# Revit family: DBLTD_TheSenatorGroup_OffcChrs_Plum_US
name_source: partatom
category: Furniture
units: mm (PartAtom-declared; Revit-internal decimal feet)

## family parameters
Always vertical = Yes
Cut with Voids When Loaded = No
Room Calculation Point = No
Shared = Yes
Work Plane-Based = No

## types (2) — shared parameters
Assembly Code = E2020200
AssetType = Movable
BIMObjectName = DBLTD_TheSenatorGroup_OfficeChairs_Plum
Category = Pr_40_50_12_57:Office chairs
Color = Defined by Material Specified
Constituents = Plastic glides with felt
DurationUnit = year
ExpectedLife = 5
Features = Soft Seating
Finish = Seat, Back and Arms Upholstered. Frame Black powder coat
FrameFinish = Black powder coat
IfcExportAs = IfcFurnitureType
IfcExportType = CHAIR
IsBuiltIn = No
Keynote = Pr_40_50_12_57
Manufacturer = The Senator Group
ManufacturerName = The Senator Group
ManufacturerURL = https://www.thesenatorgroup.com
Material = Moulded foam construction. Tubular Steel frame.
NBSDescription = Office chairs
NBSReference = 45-35-20/330
Name = OfficeChairs_Plum_TheSenatorGroup
NominalDepth = 26 "
NominalHeight = 30.5 "
PlasticAndMetalFinish = Black powder coat
ProductInformation = https://www.thesenatorgroup.com
SeatDepth = 19.25"
SeatFrameMaterial = TheSenatorGroup_Metal_Black
SeatingHeight = 17.5 "
Status = UNSET
Style = Chair
URL = https://www.thesenatorgroup.com
Uniclass2015Code = Pr_40_50_12_57
Uniclass2015Title = Office chairs
Uniclass2015Version = Products v1.15
Version = 1
WarrantyDescription = Allermuir warrants that its manufactured products are free from manufacturing defects - in materials or workmanship - for a period of five (5) years.
Allermuir will repair, or replace (at Allermuir’s sole discretion) with comparable free of charge materials/ components, any product/ component which fails under normal use in a single shift environment, as a result of a defect in the materials and/or workmanship.

Exceptions -
Non-standard product - 2 years
Screen-mounted Accessories/ Dry-wipe Boards - 2 years
Electrical and/or electronic componentry - 2 years

Exclusions - Allermuir does not warrant:
Failure due to normal “Wear and Tear”.
Natural variations in appearance of wood - its grain, figure and colour.
Changes in surface appearance resulting from exposure to light, and the natural ageing process of wood.
Changes in surface appearance resulting from the misuse of cleaning materials and methods/ damage form sharp objects/ imprinting from writing implements.
Natural variations in Leather - its marks, scars and wrinkles.
Product stored/ exposed to extreme operational conditions.
Consumable components such as Fuses/ Lights/ lamps/ transformers/etc.
Other Manufacturer’s product supplied by Allermuir (their own warranty shall apply where possible).
Non-standard fabrics/ finishes or veneers used. Allermuir only checks the manufacturing quality of Customer’s
Own Material (COM) and provides no warranty for the finish/ fabric itself.
Product which has not been installed/ moved/ reconfigured by Allermuir approved personnel.
Allermuir shall be under no liability whatsoever for any consequential damage, loss or other expenses whether arising out of contract, negligence or otherwise.
WarrantyDurationLabor = 5
WarrantyDurationParts = 5
WarrantyDurationUnit = year
zero-valued in all types: Cost, HighestSeatingHeight, LowestSeatingHeight

## per-type parameters (varying)
| type | HasArms | Model | ModelNumber | NominalLength | NominalWidth | SeatWidth | Size |
| Easy Chair without Arms | No | PLM01 | PLM01 | 23.5 " | 23.5 " | 20.75" | 30.5" (h) x 23.5" (w) x 26" (d) |
| Easy Chair with Arms | Yes | PLM02 | PLM02 | 28.25 " | 28.25 " | 19.25" | 30.5" (h) x 28.25" (w) x 26" (d) |

note: column(s) folded — value = type name in every type: Description, ModelReference, Type Comments

## geometry (parser evidence)
native form markers: Sweep x2
no freeform markers — native parametric forms only
